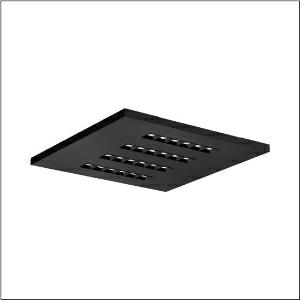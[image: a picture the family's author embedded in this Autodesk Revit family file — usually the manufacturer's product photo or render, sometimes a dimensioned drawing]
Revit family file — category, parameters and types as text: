
# Revit family: silica_r__21_square_51mx6kdu34b_186d
name_source: partatom
category: Lighting Fixtures
units: mm (PartAtom-declared; Revit-internal decimal feet)

## family parameters
Cut with Voids When Loaded = No
Host = Face
Light Source = No
Part Type = Normal
Room Calculation Point = No
Round Connector Dimension = Use Diameter
Shared = No

## types (1)
- --- (1 x LED, 4600 lm, 31.9 W, 3000K)
    Apparent Load = 32 VA
    CIE Flux Codes = 86 100 100 100 100
    Color Rendering = 80
    Color Temperature = 3000K
    Default Elevation = 1800 mm
    Description = Silica® 21 Square, office luminaire, primary light control with lens, of PMMA, primary anti-glare with reflector, of PC, black, CAT 2 (L<= 3000cd/m²), light emission: direct distribution, primary light characteristic: symmetric, installation type: lay-in mounting, LED, rated luminous flux: 4.600lm, luminous efficacy: 144lm/W, light colour: 830, colour temperature: 3000K, with terminal, 5-pole, mains connection: 220..240V, AC, 50/60Hz, rated input power: 31.9W, luminaire housing, of aluminium, jet black (RAL 9005), module: M625, length: 622mm, width: 622mm, height: 33mm, protection rating (complete): IP20, insulation class (complete): insulation class I (protective earthing), certification: CE, permissible operating ambient temperature: -20..+40°C, standard: EN 50419, packaging unit: 1 piece
    Height = 0 mm  [stored 0 ft]
    Lamp = 1 x LED
    Lamp Light Flux = 4600 lm
    Lamp Power = 31.9 W
    Lamp count = 1
    Length = 622 mm
    Luminous efficacy = 144 lm/W
    Manufacturer = Siteco
    ModVariant = No
    Model = 51MX6KDU34B
    Mounting Place = Ceiling
    Mounting Type = Recessed
    Number of Poles = 1
    OnlyDefault = Yes
    Power Factor = 1
    Product Name = Silica® 21 Square
    Product group = office luminaire | ceiling recessed
    ProductGroupID = 401
    Protection Class = Protection class I
    Protection Degree = IP 20
    RLX_Detail_Level = 1
    RLX_Emergency_Light_Flux = 0 lm
    RLX_Emergency_Type = 0
    RLX_Emergency_Type_DB = No
    RlxData = <blob elided: 24937 chars, md5=b281191f>
    Socket = socket
    Standby Power = 0 W
    System Light Flux = 4600 lm
    System Power = 32 W
    Type Comments = factory setting: luminous flux: 100 % | dim-lin: 254 | 430 mA
    Type Image = l_1275204.jpg
    URL = http://relux.com
    VarID = @adj_036217
    Voltage = 0 V
    Weight = 0.00 kg
    Width = 622 mm

note: [stored X ft] marks values corroborated as IEEE doubles in the binary element streams (Revit-internal decimal feet)

## geometry (parser evidence)
native form markers: Blend x4, Sweep x11
no freeform markers — native parametric forms only
